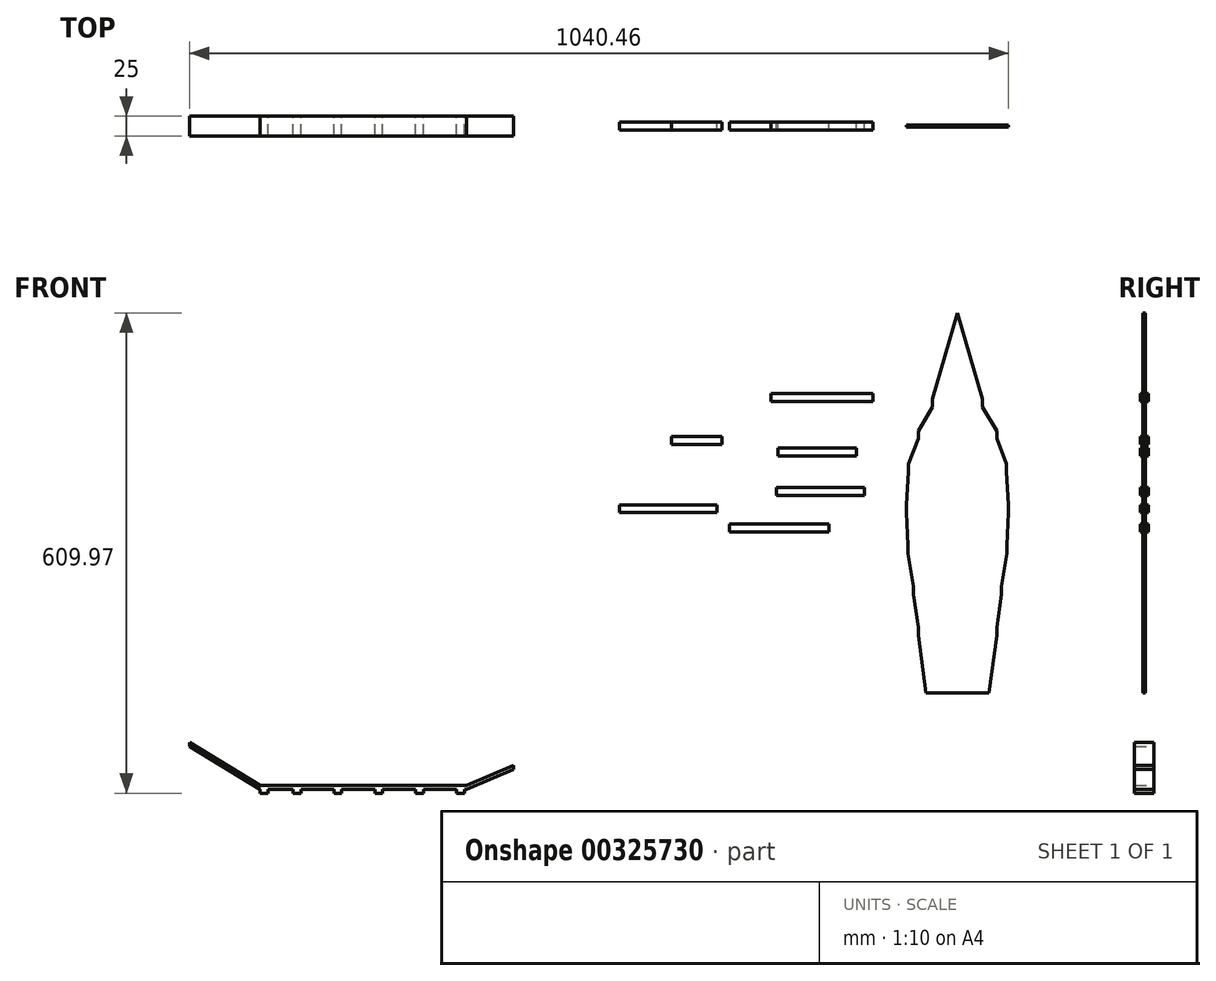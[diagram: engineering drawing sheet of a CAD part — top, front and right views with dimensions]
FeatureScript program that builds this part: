
annotation { "Feature Type Name" : "Feature", "Feature Type Description" : "" }
export const myFeature = defineFeature(function(context is Context, id is Id, definition is map)
    precondition{}
    {
        {
            var Q0;
            Q0=qCreatedBy(makeId("Front.planeOp"),FACE);
            var sketch = newSketch(context, id + "F0", { "sketchPlane" : qUnion([Q0])});
            skLineSegment(sketch, "E0.bottom", {"start": v(-236.59, 146.25) * mm, "end": v(-107.05, 146.25) * mm});
            skLineSegment(sketch, "E0.top", {"start": v(-236.59, 136.25) * mm, "end": v(-107.05, 136.25) * mm});
            skLineSegment(sketch, "E0.left", {"start": v(-236.59, 146.25) * mm, "end": v(-236.59, 136.25) * mm});
            skLineSegment(sketch, "E0.right", {"start": v(-107.05, 146.25) * mm, "end": v(-107.05, 136.25) * mm});
            skPoint(sketch, "E0.middle", {"position": v(-171.82, 141.25) * mm});
            skLineSegment(sketch, "E1.bottom", {"start": v(-228.02, 66.85) * mm, "end": v(-128.24, 66.85) * mm});
            skLineSegment(sketch, "E1.top", {"start": v(-228.02, 76.85) * mm, "end": v(-128.24, 76.85) * mm});
            skLineSegment(sketch, "E1.left", {"start": v(-228.02, 66.85) * mm, "end": v(-228.02, 76.85) * mm});
            skLineSegment(sketch, "E1.right", {"start": v(-128.24, 66.85) * mm, "end": v(-128.24, 76.85) * mm});
            skPoint(sketch, "E1.middle", {"position": v(-178.13, 71.85) * mm});
            skLineSegment(sketch, "E2.bottom", {"start": v(-118.1, 16.94) * mm, "end": v(-230.13, 16.94) * mm});
            skLineSegment(sketch, "E2.top", {"start": v(-118.1, 26.94) * mm, "end": v(-230.13, 26.94) * mm});
            skLineSegment(sketch, "E2.left", {"start": v(-118.1, 16.94) * mm, "end": v(-118.1, 26.94) * mm});
            skLineSegment(sketch, "E2.right", {"start": v(-230.13, 16.94) * mm, "end": v(-230.13, 26.94) * mm});
            skPoint(sketch, "E2.middle", {"position": v(-174.11, 21.94) * mm});
            skLineSegment(sketch, "E3.bottom", {"start": v(-163.3, -29.52) * mm, "end": v(-289.32, -29.52) * mm});
            skLineSegment(sketch, "E3.top", {"start": v(-163.3, -19.52) * mm, "end": v(-289.32, -19.52) * mm});
            skLineSegment(sketch, "E3.left", {"start": v(-163.3, -29.52) * mm, "end": v(-163.3, -19.52) * mm});
            skLineSegment(sketch, "E3.right", {"start": v(-289.32, -29.52) * mm, "end": v(-289.32, -19.52) * mm});
            skPoint(sketch, "E3.middle", {"position": v(-226.31, -24.52) * mm});
            skLineSegment(sketch, "E4.bottom", {"start": v(-299.01, 81.55) * mm, "end": v(-363.01, 81.55) * mm});
            skLineSegment(sketch, "E4.top", {"start": v(-299.01, 91.55) * mm, "end": v(-363.01, 91.55) * mm});
            skLineSegment(sketch, "E4.left", {"start": v(-299.01, 81.55) * mm, "end": v(-299.01, 91.55) * mm});
            skLineSegment(sketch, "E4.right", {"start": v(-363.01, 81.55) * mm, "end": v(-363.01, 91.55) * mm});
            skPoint(sketch, "E4.middle", {"position": v(-331.01, 86.55) * mm});
            skLineSegment(sketch, "E5.bottom", {"start": v(-305.2, -5) * mm, "end": v(-429.47, -5) * mm});
            skLineSegment(sketch, "E5.top", {"start": v(-305.2, 5) * mm, "end": v(-429.47, 5) * mm});
            skLineSegment(sketch, "E5.left", {"start": v(-305.2, -5) * mm, "end": v(-305.2, 5) * mm});
            skLineSegment(sketch, "E5.right", {"start": v(-429.47, -5) * mm, "end": v(-429.47, 5) * mm});
            skPoint(sketch, "E5.middle", {"position": v(-367.34, 0) * mm});
            skLineSegment(sketch, "E6", {"start": v(0, -224.71) * mm, "end": v(0, 248.52) * mm, "construction": true});
            skLineSegment(sketch, "E7.bottom", {"start": v(-64.77, -5) * mm, "end": v(64.77, -5) * mm});
            skLineSegment(sketch, "E7.top", {"start": v(-64.77, 5) * mm, "end": v(64.77, 5) * mm});
            skLineSegment(sketch, "E7.left", {"start": v(-64.77, -5) * mm, "end": v(-64.77, 5) * mm});
            skLineSegment(sketch, "E7.right", {"start": v(64.77, -5) * mm, "end": v(64.77, 5) * mm});
            skPoint(sketch, "E7.middle", {"position": v(0, 0) * mm});
            skLineSegment(sketch, "E8.bottom", {"start": v(-40.18, -243.89) * mm, "end": v(40.18, -243.89) * mm});
            skLineSegment(sketch, "E8.top", {"start": v(-40.18, -233.89) * mm, "end": v(40.18, -233.89) * mm});
            skLineSegment(sketch, "E8.left", {"start": v(-40.18, -243.89) * mm, "end": v(-40.18, -233.89) * mm});
            skLineSegment(sketch, "E8.right", {"start": v(40.18, -243.89) * mm, "end": v(40.18, -233.89) * mm});
            skPoint(sketch, "E8.middle", {"position": v(0, -238.89) * mm});
            skLineSegment(sketch, "E9.bottom", {"start": v(-49.89, -161) * mm, "end": v(49.89, -161) * mm});
            skLineSegment(sketch, "E9.top", {"start": v(-49.89, -151) * mm, "end": v(49.89, -151) * mm});
            skLineSegment(sketch, "E9.left", {"start": v(-49.89, -161) * mm, "end": v(-49.89, -151) * mm});
            skLineSegment(sketch, "E9.right", {"start": v(49.89, -161) * mm, "end": v(49.89, -151) * mm});
            skPoint(sketch, "E9.middle", {"position": v(0, -156) * mm});
            skLineSegment(sketch, "E10.bottom", {"start": v(-56.02, -109) * mm, "end": v(56.02, -109) * mm});
            skLineSegment(sketch, "E10.top", {"start": v(-56.02, -99) * mm, "end": v(56.02, -99) * mm});
            skLineSegment(sketch, "E10.left", {"start": v(-56.02, -109) * mm, "end": v(-56.02, -99) * mm});
            skLineSegment(sketch, "E10.right", {"start": v(56.02, -109) * mm, "end": v(56.02, -99) * mm});
            skPoint(sketch, "E10.middle", {"position": v(0, -104) * mm});
            skLineSegment(sketch, "E11.bottom", {"start": v(-63, -57) * mm, "end": v(63, -57) * mm});
            skLineSegment(sketch, "E11.top", {"start": v(-63, -47) * mm, "end": v(63, -47) * mm});
            skLineSegment(sketch, "E11.left", {"start": v(-63, -57) * mm, "end": v(-63, -47) * mm});
            skLineSegment(sketch, "E11.right", {"start": v(63, -57) * mm, "end": v(63, -47) * mm});
            skPoint(sketch, "E11.middle", {"position": v(0, -52) * mm});
            skLineSegment(sketch, "E12.bottom", {"start": v(-62.13, 47) * mm, "end": v(62.13, 47) * mm});
            skLineSegment(sketch, "E12.top", {"start": v(-62.13, 57) * mm, "end": v(62.13, 57) * mm});
            skLineSegment(sketch, "E12.left", {"start": v(-62.13, 47) * mm, "end": v(-62.13, 57) * mm});
            skLineSegment(sketch, "E12.right", {"start": v(62.13, 47) * mm, "end": v(62.13, 57) * mm});
            skPoint(sketch, "E12.middle", {"position": v(0, 52) * mm});
            skLineSegment(sketch, "E13.bottom", {"start": v(-49.89, 89) * mm, "end": v(49.89, 89) * mm});
            skLineSegment(sketch, "E13.top", {"start": v(-49.89, 99) * mm, "end": v(49.89, 99) * mm});
            skLineSegment(sketch, "E13.left", {"start": v(-49.89, 89) * mm, "end": v(-49.89, 99) * mm});
            skLineSegment(sketch, "E13.right", {"start": v(49.89, 89) * mm, "end": v(49.89, 99) * mm});
            skPoint(sketch, "E13.middle", {"position": v(0, 94) * mm});
            skLineSegment(sketch, "E14.bottom", {"start": v(-32, 129.2) * mm, "end": v(32, 129.2) * mm});
            skLineSegment(sketch, "E14.top", {"start": v(-32, 139.2) * mm, "end": v(32, 139.2) * mm});
            skLineSegment(sketch, "E14.left", {"start": v(-32, 129.2) * mm, "end": v(-32, 139.2) * mm});
            skLineSegment(sketch, "E14.right", {"start": v(32, 129.2) * mm, "end": v(32, 139.2) * mm});
            skPoint(sketch, "E14.middle", {"position": v(0, 134.2) * mm});
            skLineSegment(sketch, "E15", {"start": v(-40.18, -233.89) * mm, "end": v(-49.89, -161) * mm});
            skLineSegment(sketch, "E16", {"start": v(40.18, -233.89) * mm, "end": v(49.89, -161) * mm});
            skLineSegment(sketch, "E17", {"start": v(-49.89, -151) * mm, "end": v(-56.02, -109) * mm});
            skLineSegment(sketch, "E18", {"start": v(49.89, -151) * mm, "end": v(56.02, -109) * mm});
            skLineSegment(sketch, "E19", {"start": v(56.02, -99) * mm, "end": v(63, -57) * mm});
            skLineSegment(sketch, "E20", {"start": v(-56.02, -99) * mm, "end": v(-63, -57) * mm});
            skLineSegment(sketch, "E21", {"start": v(-63, -47) * mm, "end": v(-64.77, -5) * mm});
            skLineSegment(sketch, "E22", {"start": v(64.77, -5) * mm, "end": v(63, -47) * mm});
            skLineSegment(sketch, "E23", {"start": v(64.77, 5) * mm, "end": v(62.13, 47) * mm});
            skLineSegment(sketch, "E24", {"start": v(-64.77, 5) * mm, "end": v(-62.13, 47) * mm});
            skLineSegment(sketch, "E25", {"start": v(-62.13, 57) * mm, "end": v(-49.89, 89) * mm});
            skLineSegment(sketch, "E26", {"start": v(62.14, 57) * mm, "end": v(49.89, 89) * mm});
            skLineSegment(sketch, "E27", {"start": v(49.89, 99) * mm, "end": v(32, 129.2) * mm});
            skLineSegment(sketch, "E28", {"start": v(-49.89, 99) * mm, "end": v(-32, 129.2) * mm});
            skLineSegment(sketch, "E29", {"start": v(-32, 139.2) * mm, "end": v(0, 248.52) * mm});
            skLineSegment(sketch, "E30", {"start": v(32, 139.2) * mm, "end": v(0, 248.52) * mm});
            skLineSegment(sketch, "E31", {"start": v(49.89, 99) * mm, "end": v(32, 139.2) * mm});
            skLineSegment(sketch, "E32", {"start": v(-49.89, 99) * mm, "end": v(-62.13, 57) * mm});
            skLineSegment(sketch, "E33", {"start": v(62.13, 57) * mm, "end": v(49.89, 99) * mm});
            skLineSegment(sketch, "E34", {"start": v(-49.89, 99) * mm, "end": v(-32, 139.2) * mm});
            skLineSegment(sketch, "E35", {"start": v(-636.52, -143.35) * mm, "end": v(-374.52, -143.35) * mm});
            skLineSegment(sketch, "E36", {"start": v(-636.52, -143.35) * mm, "end": v(-726.43, -88.93) * mm});
            skLineSegment(sketch, "E37", {"start": v(-374.52, -143.35) * mm, "end": v(-314.52, -117.88) * mm});
            skLineSegment(sketch, "E38.0", {"start": v(-633.93, -139.07) * mm, "end": v(-723.84, -84.65) * mm});
            skLineSegment(sketch, "E39.0", {"start": v(-636.52, -138.35) * mm, "end": v(-374.52, -138.35) * mm});
            skLineSegment(sketch, "E40.0", {"start": v(-376.47, -138.75) * mm, "end": v(-316.47, -113.28) * mm});
            skLineSegment(sketch, "E41", {"start": v(-316.47, -113.28) * mm, "end": v(-314.52, -117.88) * mm});
            skLineSegment(sketch, "E42", {"start": v(-723.84, -84.65) * mm, "end": v(-726.43, -88.93) * mm});
            skPoint(sketch, "E43", {"position": v(-675.35, -119.84) * mm});
            skLineSegment(sketch, "E44", {"start": v(-665.35, -125.9) * mm, "end": v(-675.35, -119.84) * mm});
            skPoint(sketch, "E45", {"position": v(-636.52, -143.35) * mm});
            skPoint(sketch, "E46", {"position": v(-626.52, -143.35) * mm});
            skPoint(sketch, "E47", {"position": v(-636.52, -148.35) * mm});
            skPoint(sketch, "E48", {"position": v(-626.52, -148.35) * mm});
            skLineSegment(sketch, "E49", {"start": v(-636.52, -143.35) * mm, "end": v(-636.52, -148.35) * mm});
            skLineSegment(sketch, "E50", {"start": v(-636.52, -148.35) * mm, "end": v(-626.52, -148.35) * mm});
            skLineSegment(sketch, "E51", {"start": v(-626.52, -143.35) * mm, "end": v(-626.52, -148.35) * mm});
            skPoint(sketch, "E52", {"position": v(-594.82, -143.35) * mm});
            skPoint(sketch, "E53", {"position": v(-584.82, -143.35) * mm});
            skPoint(sketch, "E54", {"position": v(-594.82, -148.35) * mm});
            skPoint(sketch, "E55", {"position": v(-584.82, -148.35) * mm});
            skLineSegment(sketch, "E56", {"start": v(-584.82, -148.35) * mm, "end": v(-594.82, -148.35) * mm});
            skLineSegment(sketch, "E57", {"start": v(-594.82, -143.35) * mm, "end": v(-594.82, -148.35) * mm});
            skLineSegment(sketch, "E58", {"start": v(-584.82, -148.35) * mm, "end": v(-584.82, -143.35) * mm});
            skPoint(sketch, "E59", {"position": v(-542.82, -143.35) * mm});
            skPoint(sketch, "E60", {"position": v(-532.82, -143.35) * mm});
            skPoint(sketch, "E61", {"position": v(-542.82, -148.35) * mm});
            skPoint(sketch, "E62", {"position": v(-532.82, -148.35) * mm});
            skLineSegment(sketch, "E63", {"start": v(-542.82, -143.35) * mm, "end": v(-542.82, -148.35) * mm});
            skLineSegment(sketch, "E64", {"start": v(-542.82, -148.35) * mm, "end": v(-532.82, -148.35) * mm});
            skLineSegment(sketch, "E65", {"start": v(-532.82, -143.35) * mm, "end": v(-532.82, -148.35) * mm});
            skPoint(sketch, "E66", {"position": v(-490.82, -143.35) * mm});
            skPoint(sketch, "E67", {"position": v(-480.82, -143.35) * mm});
            skPoint(sketch, "E68", {"position": v(-490.82, -148.35) * mm});
            skPoint(sketch, "E69", {"position": v(-480.82, -148.35) * mm});
            skLineSegment(sketch, "E70", {"start": v(-490.82, -143.35) * mm, "end": v(-490.82, -148.35) * mm});
            skLineSegment(sketch, "E71", {"start": v(-480.82, -148.35) * mm, "end": v(-490.82, -148.35) * mm});
            skLineSegment(sketch, "E72", {"start": v(-480.82, -143.35) * mm, "end": v(-480.82, -148.35) * mm});
            skPoint(sketch, "E73", {"position": v(-438.82, -143.35) * mm});
            skPoint(sketch, "E74", {"position": v(-428.82, -143.35) * mm});
            skPoint(sketch, "E75", {"position": v(-438.82, -148.35) * mm});
            skPoint(sketch, "E76", {"position": v(-428.82, -148.35) * mm});
            skLineSegment(sketch, "E77", {"start": v(-428.82, -143.35) * mm, "end": v(-428.82, -148.35) * mm});
            skLineSegment(sketch, "E78", {"start": v(-438.82, -148.35) * mm, "end": v(-438.82, -143.35) * mm});
            skLineSegment(sketch, "E79", {"start": v(-438.82, -148.35) * mm, "end": v(-428.82, -148.35) * mm});
            skPoint(sketch, "E80", {"position": v(-386.82, -143.35) * mm});
            skPoint(sketch, "E81", {"position": v(-376.82, -143.35) * mm});
            skPoint(sketch, "E82", {"position": v(-386.82, -148.35) * mm});
            skPoint(sketch, "E83", {"position": v(-376.82, -148.35) * mm});
            skLineSegment(sketch, "E84", {"start": v(-386.82, -143.35) * mm, "end": v(-386.82, -148.35) * mm});
            skLineSegment(sketch, "E85", {"start": v(-386.82, -148.35) * mm, "end": v(-376.82, -148.35) * mm});
            skLineSegment(sketch, "E86", {"start": v(-376.82, -143.35) * mm, "end": v(-376.82, -148.35) * mm});
            skLineSegment(sketch, "E87", {"start": v(-511.82, -138.35) * mm, "end": v(-511.82, -143.35) * mm});
            skPoint(sketch, "E88", {"position": v(-459.7, -138.35) * mm});
            skPoint(sketch, "E89", {"position": v(-563.1, -138.35) * mm});
            skLineSegment(sketch, "E90", {"start": v(-376.47, -138.75) * mm, "end": v(-376.82, -143.35) * mm});
            skLineSegment(sketch, "E91", {"start": v(-376.82, -143.35) * mm, "end": v(-511.82, -143.35) * mm});
            skLineSegment(sketch, "E92", {"start": v(-511.82, -138.35) * mm, "end": v(-376.47, -138.75) * mm});
            skLineSegment(sketch, "E93", {"start": v(-511.82, -143.35) * mm, "end": v(-636.52, -143.35) * mm});
            skLineSegment(sketch, "E94", {"start": v(-636.52, -138.35) * mm, "end": v(-636.52, -143.35) * mm});
            skLineSegment(sketch, "E95", {"start": v(-636.52, -138.35) * mm, "end": v(-511.82, -138.35) * mm});
            skLineSegment(sketch, "E96", {"start": v(-584.82, -138.35) * mm, "end": v(-438.82, -138.35) * mm});
            skPoint(sketch, "E97", {"position": v(-584.82, -138.35) * mm});
            skPoint(sketch, "E98", {"position": v(-438.82, -138.35) * mm});
            skLineSegment(sketch, "E99.bottom", {"start": v(-754.78, -356.45) * mm, "end": v(-885.78, -356.45) * mm});
            skLineSegment(sketch, "E99.top", {"start": v(-754.78, -351.45) * mm, "end": v(-885.78, -351.45) * mm});
            skLineSegment(sketch, "E99.left", {"start": v(-754.78, -356.45) * mm, "end": v(-754.78, -351.45) * mm});
            skLineSegment(sketch, "E99.right", {"start": v(-885.78, -356.45) * mm, "end": v(-885.78, -351.45) * mm});
            skPoint(sketch, "E99.middle", {"position": v(-820.28, -353.95) * mm});
            skLineSegment(sketch, "E100.bottom", {"start": v(-623.78, -356.45) * mm, "end": v(-754.78, -356.45) * mm});
            skLineSegment(sketch, "E100.top", {"start": v(-623.78, -351.45) * mm, "end": v(-754.78, -351.45) * mm});
            skLineSegment(sketch, "E100.left", {"start": v(-623.78, -356.45) * mm, "end": v(-623.78, -351.45) * mm});
            skPoint(sketch, "E100.middle", {"position": v(-689.28, -353.95) * mm});
            skPoint(sketch, "E101", {"position": v(-623.78, -356.45) * mm});
            skLineSegment(sketch, "E102", {"start": v(-623.78, -356.45) * mm, "end": v(-563.78, -330.98) * mm});
            skLineSegment(sketch, "E103", {"start": v(-623.78, -351.45) * mm, "end": v(-563.78, -325.98) * mm});
            skLineSegment(sketch, "E104", {"start": v(-563.78, -325.98) * mm, "end": v(-563.78, -330.98) * mm});
            skLineSegment(sketch, "E105", {"start": v(-885.78, -356.45) * mm, "end": v(-975.7, -302.03) * mm});
            skLineSegment(sketch, "E106", {"start": v(-885.78, -351.45) * mm, "end": v(-975.7, -297.03) * mm});
            skLineSegment(sketch, "E107", {"start": v(-975.7, -297.03) * mm, "end": v(-975.7, -302.03) * mm});
            skLineSegment(sketch, "E108.bottom", {"start": v(-875.78, -361.45) * mm, "end": v(-885.78, -361.45) * mm});
            skLineSegment(sketch, "E108.top", {"start": v(-875.78, -356.45) * mm, "end": v(-885.78, -356.45) * mm});
            skLineSegment(sketch, "E108.left", {"start": v(-875.78, -361.45) * mm, "end": v(-875.78, -356.45) * mm});
            skLineSegment(sketch, "E108.right", {"start": v(-885.78, -361.45) * mm, "end": v(-885.78, -356.45) * mm});
            skPoint(sketch, "E108.middle", {"position": v(-880.78, -358.95) * mm});
            skLineSegment(sketch, "E109.bottom", {"start": v(-678.08, -361.45) * mm, "end": v(-688.08, -361.45) * mm});
            skLineSegment(sketch, "E109.top", {"start": v(-678.08, -356.45) * mm, "end": v(-688.08, -356.45) * mm});
            skLineSegment(sketch, "E109.left", {"start": v(-678.08, -361.45) * mm, "end": v(-678.08, -356.45) * mm});
            skLineSegment(sketch, "E109.right", {"start": v(-688.08, -361.45) * mm, "end": v(-688.08, -356.45) * mm});
            skLineSegment(sketch, "E110.bottom", {"start": v(-730.08, -361.45) * mm, "end": v(-740.08, -361.45) * mm});
            skLineSegment(sketch, "E110.top", {"start": v(-730.08, -356.45) * mm, "end": v(-740.08, -356.45) * mm});
            skLineSegment(sketch, "E110.left", {"start": v(-730.08, -361.45) * mm, "end": v(-730.08, -356.45) * mm});
            skLineSegment(sketch, "E110.right", {"start": v(-740.08, -361.45) * mm, "end": v(-740.08, -356.45) * mm});
            skLineSegment(sketch, "E111.bottom", {"start": v(-782.08, -361.45) * mm, "end": v(-792.08, -361.45) * mm});
            skLineSegment(sketch, "E111.top", {"start": v(-782.08, -356.45) * mm, "end": v(-792.08, -356.45) * mm});
            skLineSegment(sketch, "E111.left", {"start": v(-782.08, -361.45) * mm, "end": v(-782.08, -356.45) * mm});
            skLineSegment(sketch, "E111.right", {"start": v(-792.08, -361.45) * mm, "end": v(-792.08, -356.45) * mm});
            skLineSegment(sketch, "E112.bottom", {"start": v(-834.08, -361.45) * mm, "end": v(-844.08, -361.45) * mm});
            skLineSegment(sketch, "E112.top", {"start": v(-834.08, -356.45) * mm, "end": v(-844.08, -356.45) * mm});
            skLineSegment(sketch, "E112.left", {"start": v(-834.08, -361.45) * mm, "end": v(-834.08, -356.45) * mm});
            skLineSegment(sketch, "E112.right", {"start": v(-844.08, -361.45) * mm, "end": v(-844.08, -356.45) * mm});
            skLineSegment(sketch, "E113.bottom", {"start": v(-626.08, -361.45) * mm, "end": v(-636.08, -361.45) * mm});
            skLineSegment(sketch, "E113.top", {"start": v(-626.08, -356.45) * mm, "end": v(-636.08, -356.45) * mm});
            skLineSegment(sketch, "E113.left", {"start": v(-626.08, -361.45) * mm, "end": v(-626.08, -356.45) * mm});
            skLineSegment(sketch, "E113.right", {"start": v(-636.08, -361.45) * mm, "end": v(-636.08, -356.45) * mm});
            skPoint(sketch, "E114", {"position": v(-626.08, -356.45) * mm});
            skPoint(sketch, "E115", {"position": v(-844.08, -356.45) * mm});
            skPoint(sketch, "E116", {"position": v(-792.08, -356.45) * mm});
            skPoint(sketch, "E117", {"position": v(-740.08, -356.45) * mm});
            skPoint(sketch, "E118", {"position": v(-688.08, -356.45) * mm});
            skPoint(sketch, "E119", {"position": v(-820.28, -351.45) * mm});
            skPoint(sketch, "E120", {"position": v(-689.28, -351.45) * mm});
            skSolve(sketch);
        }
        {
            var Q0;
            Q0=makeQuery(id+"F0.imprint","IMPRINT",FACE,{"disambiguationData":[TD([[makeQuery(id+"F0.imprint","IMPRINT",EDGE,{"derivedFrom":sQuery(id+"F0.wireOp",EDGE,"E3.bottom")}),-1.0]])]});
            var Q1;
            Q1=makeQuery(id+"F0.imprint","IMPRINT",FACE,{"disambiguationData":[TD([[makeQuery(id+"F0.imprint","IMPRINT",EDGE,{"derivedFrom":sQuery(id+"F0.wireOp",EDGE,"E4.bottom")}),-1.0]])]});
            var Q2;
            Q2=makeQuery(id+"F0.imprint","IMPRINT",FACE,{"disambiguationData":[TD([[makeQuery(id+"F0.imprint","IMPRINT",EDGE,{"derivedFrom":sQuery(id+"F0.wireOp",EDGE,"E5.bottom")}),-1.0]])]});
            var Q3;
            Q3=makeQuery(id+"F0.imprint","IMPRINT",FACE,{"disambiguationData":[TD([[makeQuery(id+"F0.imprint","IMPRINT",EDGE,{"derivedFrom":sQuery(id+"F0.wireOp",EDGE,"E2.bottom")}),-1.0]])]});
            var Q4;
            Q4=makeQuery(id+"F0.imprint","IMPRINT",FACE,{"disambiguationData":[TD([[makeQuery(id+"F0.imprint","IMPRINT",EDGE,{"derivedFrom":sQuery(id+"F0.wireOp",EDGE,"E1.bottom")}),1.0]])]});
            var Q5;
            Q5=makeQuery(id+"F0.imprint","IMPRINT",FACE,{"disambiguationData":[TD([[makeQuery(id+"F0.imprint","IMPRINT",EDGE,{"derivedFrom":sQuery(id+"F0.wireOp",EDGE,"E0.bottom")}),-1.0]])]});
            extrude(context, id + "F1", {"entities" : qUnion([Q0, Q1, Q2, Q3, Q4, Q5]), "endBound" : BoundingType.SYMMETRIC, "depth" : 10 * mm});
        }
        {
            var Q0;
            Q0=makeQuery(id+"F0.imprint","IMPRINT",FACE,{"disambiguationData":[TD([[makeQuery(id+"F0.imprint","IMPRINT",EDGE,{"derivedFrom":sQuery(id+"F0.wireOp",EDGE,"E12.top")}),1.0]])]});
            var Q1;
            Q1=makeQuery(id+"F0.imprint","IMPRINT",FACE,{"disambiguationData":[TD([[makeQuery(id+"F0.imprint","IMPRINT",EDGE,{"derivedFrom":sQuery(id+"F0.wireOp",EDGE,"E14.top")}),1.0]])]});
            var Q2;
            Q2=makeQuery(id+"F0.imprint","IMPRINT",FACE,{"disambiguationData":[TD([[makeQuery(id+"F0.imprint","IMPRINT",EDGE,{"derivedFrom":sQuery(id+"F0.wireOp",EDGE,"E13.top")}),1.0]])]});
            var Q3;
            Q3=makeQuery(id+"F0.imprint","IMPRINT",FACE,{"disambiguationData":[TD([[makeQuery(id+"F0.imprint","IMPRINT",EDGE,{"derivedFrom":sQuery(id+"F0.wireOp",EDGE,"E14.bottom")}),1.0]])]});
            var Q4;
            Q4=makeQuery(id+"F0.imprint","IMPRINT",FACE,{"disambiguationData":[TD([[makeQuery(id+"F0.imprint","IMPRINT",EDGE,{"derivedFrom":sQuery(id+"F0.wireOp",EDGE,"E13.bottom")}),1.0]])]});
            var Q5;
            Q5=makeQuery(id+"F0.imprint","IMPRINT",FACE,{"disambiguationData":[TD([[makeQuery(id+"F0.imprint","IMPRINT",EDGE,{"derivedFrom":sQuery(id+"F0.wireOp",EDGE,"E12.bottom")}),1.0]])]});
            var Q6;
            Q6=makeQuery(id+"F0.imprint","IMPRINT",FACE,{"disambiguationData":[TD([[makeQuery(id+"F0.imprint","IMPRINT",EDGE,{"derivedFrom":sQuery(id+"F0.wireOp",EDGE,"E7.top")}),1.0]])]});
            var Q7;
            Q7=makeQuery(id+"F0.imprint","IMPRINT",FACE,{"disambiguationData":[TD([[makeQuery(id+"F0.imprint","IMPRINT",EDGE,{"derivedFrom":sQuery(id+"F0.wireOp",EDGE,"E11.bottom")}),1.0]])]});
            var Q8;
            Q8=makeQuery(id+"F0.imprint","IMPRINT",FACE,{"disambiguationData":[TD([[makeQuery(id+"F0.imprint","IMPRINT",EDGE,{"derivedFrom":sQuery(id+"F0.wireOp",EDGE,"E7.bottom")}),-1.0]])]});
            var Q9;
            Q9=makeQuery(id+"F0.imprint","IMPRINT",FACE,{"disambiguationData":[TD([[makeQuery(id+"F0.imprint","IMPRINT",EDGE,{"derivedFrom":sQuery(id+"F0.wireOp",EDGE,"E10.top")}),1.0]])]});
            var Q10;
            Q10=makeQuery(id+"F0.imprint","IMPRINT",FACE,{"disambiguationData":[TD([[makeQuery(id+"F0.imprint","IMPRINT",EDGE,{"derivedFrom":sQuery(id+"F0.wireOp",EDGE,"E7.bottom")}),1.0]])]});
            var Q11;
            Q11=makeQuery(id+"F0.imprint","IMPRINT",FACE,{"disambiguationData":[TD([[makeQuery(id+"F0.imprint","IMPRINT",EDGE,{"derivedFrom":sQuery(id+"F0.wireOp",EDGE,"E10.bottom")}),1.0]])]});
            var Q12;
            Q12=makeQuery(id+"F0.imprint","IMPRINT",FACE,{"disambiguationData":[TD([[makeQuery(id+"F0.imprint","IMPRINT",EDGE,{"derivedFrom":sQuery(id+"F0.wireOp",EDGE,"E9.top")}),1.0]])]});
            var Q13;
            Q13=makeQuery(id+"F0.imprint","IMPRINT",FACE,{"disambiguationData":[TD([[makeQuery(id+"F0.imprint","IMPRINT",EDGE,{"derivedFrom":sQuery(id+"F0.wireOp",EDGE,"E9.bottom")}),1.0]])]});
            var Q14;
            Q14=makeQuery(id+"F0.imprint","IMPRINT",FACE,{"disambiguationData":[TD([[makeQuery(id+"F0.imprint","IMPRINT",EDGE,{"derivedFrom":sQuery(id+"F0.wireOp",EDGE,"E8.top")}),1.0]])]});
            extrude(context, id + "F2", {"entities" : qUnion([Q0, Q1, Q2, Q3, Q4, Q5, Q6, Q7, Q8, Q9, Q10, Q11, Q12, Q13, Q14]), "endBound" : BoundingType.SYMMETRIC, "depth" : 2.87 * mm});
        }
        {
            var Q0;
            Q0=makeQuery(id+"F0.imprint","IMPRINT",FACE,{"disambiguationData":[TD([[makeQuery(id+"F0.imprint","IMPRINT",EDGE,{"derivedFrom":sQuery(id+"F0.wireOp",EDGE,"E99.right")}),1.0]])]});
            var Q1;
            Q1=makeQuery(id+"F0.imprint","IMPRINT",FACE,{"disambiguationData":[TD([[makeQuery(id+"F0.imprint","IMPRINT",EDGE,{"derivedFrom":sQuery(id+"F0.wireOp",EDGE,"E108.bottom")}),-1.0]])]});
            var Q2;
            Q2=makeQuery(id+"F0.imprint","IMPRINT",FACE,{"disambiguationData":[TD([[makeQuery(id+"F0.imprint","IMPRINT",EDGE,{"derivedFrom":sQuery(id+"F0.wireOp",EDGE,"E99.top")}),1.0]])]});
            var Q3;
            Q3=makeQuery(id+"F0.imprint","IMPRINT",FACE,{"disambiguationData":[TD([[makeQuery(id+"F0.imprint","IMPRINT",EDGE,{"derivedFrom":sQuery(id+"F0.wireOp",EDGE,"E112.bottom")}),-1.0]])]});
            var Q4;
            Q4=makeQuery(id+"F0.imprint","IMPRINT",FACE,{"disambiguationData":[TD([[makeQuery(id+"F0.imprint","IMPRINT",EDGE,{"derivedFrom":sQuery(id+"F0.wireOp",EDGE,"E111.bottom")}),-1.0]])]});
            var Q5;
            Q5=makeQuery(id+"F0.imprint","IMPRINT",FACE,{"disambiguationData":[TD([[makeQuery(id+"F0.imprint","IMPRINT",EDGE,{"derivedFrom":sQuery(id+"F0.wireOp",EDGE,"E110.bottom")}),-1.0]])]});
            var Q6;
            Q6=makeQuery(id+"F0.imprint","IMPRINT",FACE,{"disambiguationData":[TD([[makeQuery(id+"F0.imprint","IMPRINT",EDGE,{"derivedFrom":sQuery(id+"F0.wireOp",EDGE,"E109.bottom")}),-1.0]])]});
            var Q7;
            Q7=makeQuery(id+"F0.imprint","IMPRINT",FACE,{"disambiguationData":[TD([[makeQuery(id+"F0.imprint","IMPRINT",EDGE,{"derivedFrom":sQuery(id+"F0.wireOp",EDGE,"E113.bottom")}),-1.0]])]});
            var Q8;
            Q8=makeQuery(id+"F0.imprint","IMPRINT",FACE,{"disambiguationData":[TD([[makeQuery(id+"F0.imprint","IMPRINT",EDGE,{"derivedFrom":sQuery(id+"F0.wireOp",EDGE,"E100.top")}),1.0]])]});
            var Q9;
            Q9=makeQuery(id+"F0.imprint","IMPRINT",FACE,{"disambiguationData":[TD([[makeQuery(id+"F0.imprint","IMPRINT",EDGE,{"derivedFrom":sQuery(id+"F0.wireOp",EDGE,"E100.left")}),-1.0]])]});
            extrude(context, id + "F3", {"entities" : qUnion([Q0, Q1, Q2, Q3, Q4, Q5, Q6, Q7, Q8, Q9]), "endBound" : BoundingType.SYMMETRIC, "depth" : 25 * mm});
        }
    });
